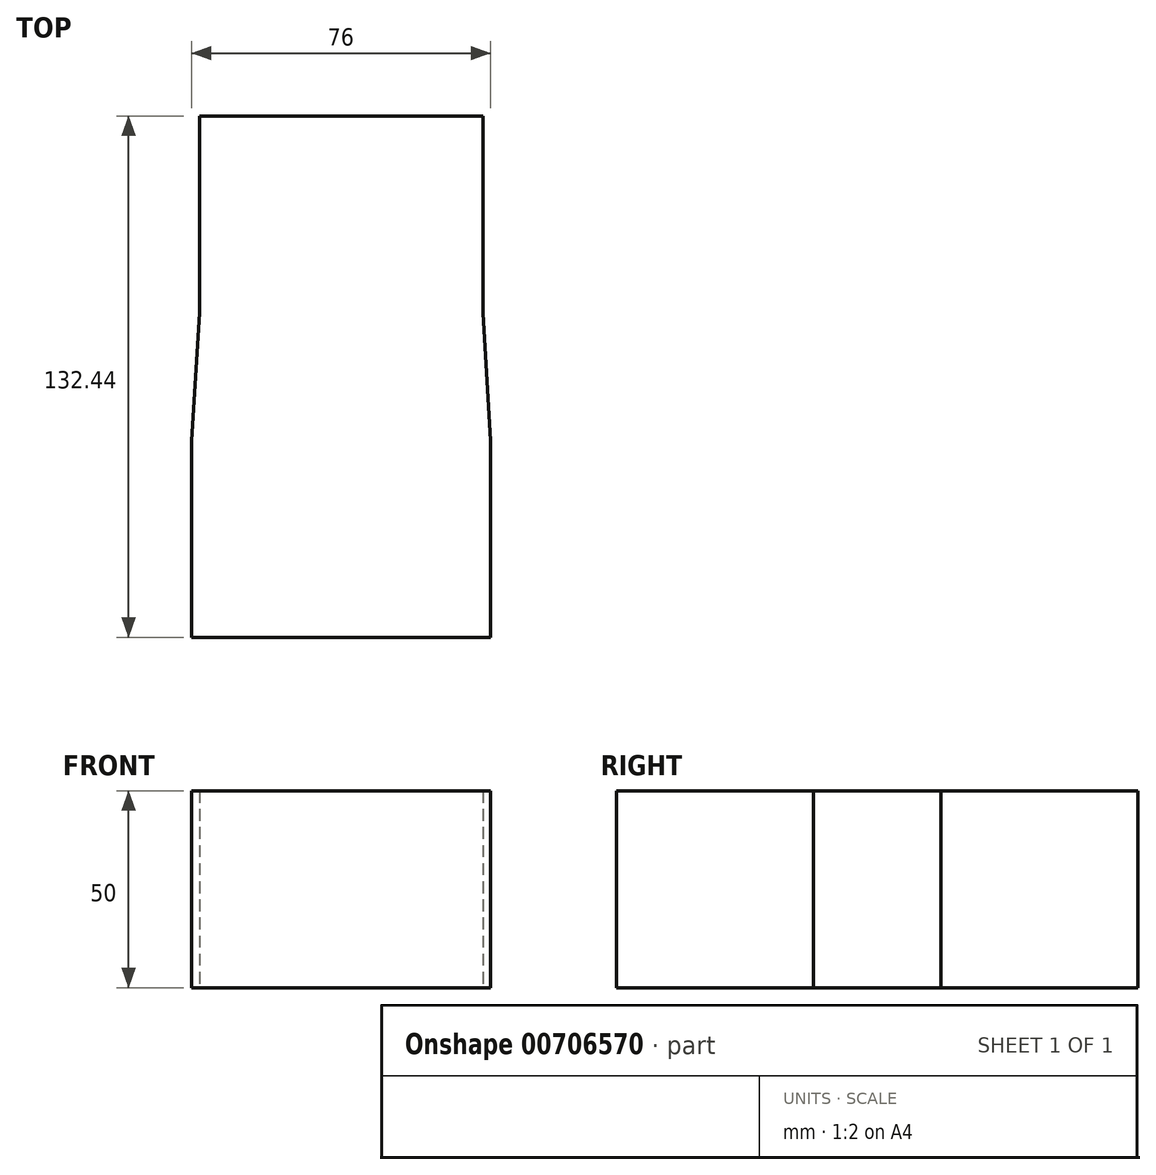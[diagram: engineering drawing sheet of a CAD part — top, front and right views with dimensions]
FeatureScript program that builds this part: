
annotation { "Feature Type Name" : "Feature", "Feature Type Description" : "" }
export const myFeature = defineFeature(function(context is Context, id is Id, definition is map)
    precondition{}
    {
        {
            var Q0;
            Q0=qCreatedBy(makeId("Top.planeOp"),FACE);
            var sketch = newSketch(context, id + "F0", { "sketchPlane" : qUnion([Q0])});
            skLineSegment(sketch, "E0", {"start": v(0, -32.44) * mm, "end": v(38, -32.44) * mm});
            skLineSegment(sketch, "E1", {"start": v(38, -32.44) * mm, "end": v(36, 0) * mm});
            skLineSegment(sketch, "E2", {"start": v(36, 0) * mm, "end": v(0, 0) * mm});
            skLineSegment(sketch, "E3", {"start": v(0, 0) * mm, "end": v(-36, 0) * mm});
            skLineSegment(sketch, "E4", {"start": v(-36, 0) * mm, "end": v(-38, -32.44) * mm});
            skLineSegment(sketch, "E5", {"start": v(-38, -32.44) * mm, "end": v(0, -32.44) * mm});
            skSolve(sketch);
        }
        {
            var Q0;
            Q0=makeQuery(id+"F0.imprint","IMPRINT",FACE,{"disambiguationData":[TD([[makeQuery(id+"F0.imprint","IMPRINT",EDGE,{"derivedFrom":sQuery(id+"F0.wireOp",EDGE,"E0")}),1.0]])]});
            extrude(context, id + "F1", {"entities" : qUnion([Q0]), "depth" : 50 * mm, "offsetDistance" : 25 * mm});
        }
        {
            var Q0;
            Q0=makeQuery(id+"F1.opExtrude","SWEPT_FACE",FACE,{"disambiguationData":[OSD([sQuery(id+"F0.wireOp",EDGE,"E2"),sQuery(id+"F0.wireOp",EDGE,"E3")])]});
            extrude(context, id + "F2", {"entities" : qUnion([Q0]), "operationType" : NewBodyOperationType.ADD, "depth" : 50 * mm, "offsetDistance" : 25 * mm});
        }
        {
            var Q0;
            Q0=makeQuery(id+"F1.opExtrude","SWEPT_FACE",FACE,{"disambiguationData":[OSD([sQuery(id+"F0.wireOp",EDGE,"E0"),sQuery(id+"F0.wireOp",EDGE,"E5")])]});
            extrude(context, id + "F3", {"entities" : qUnion([Q0]), "operationType" : NewBodyOperationType.ADD, "depth" : 50 * mm, "offsetDistance" : 25 * mm});
        }
    });
